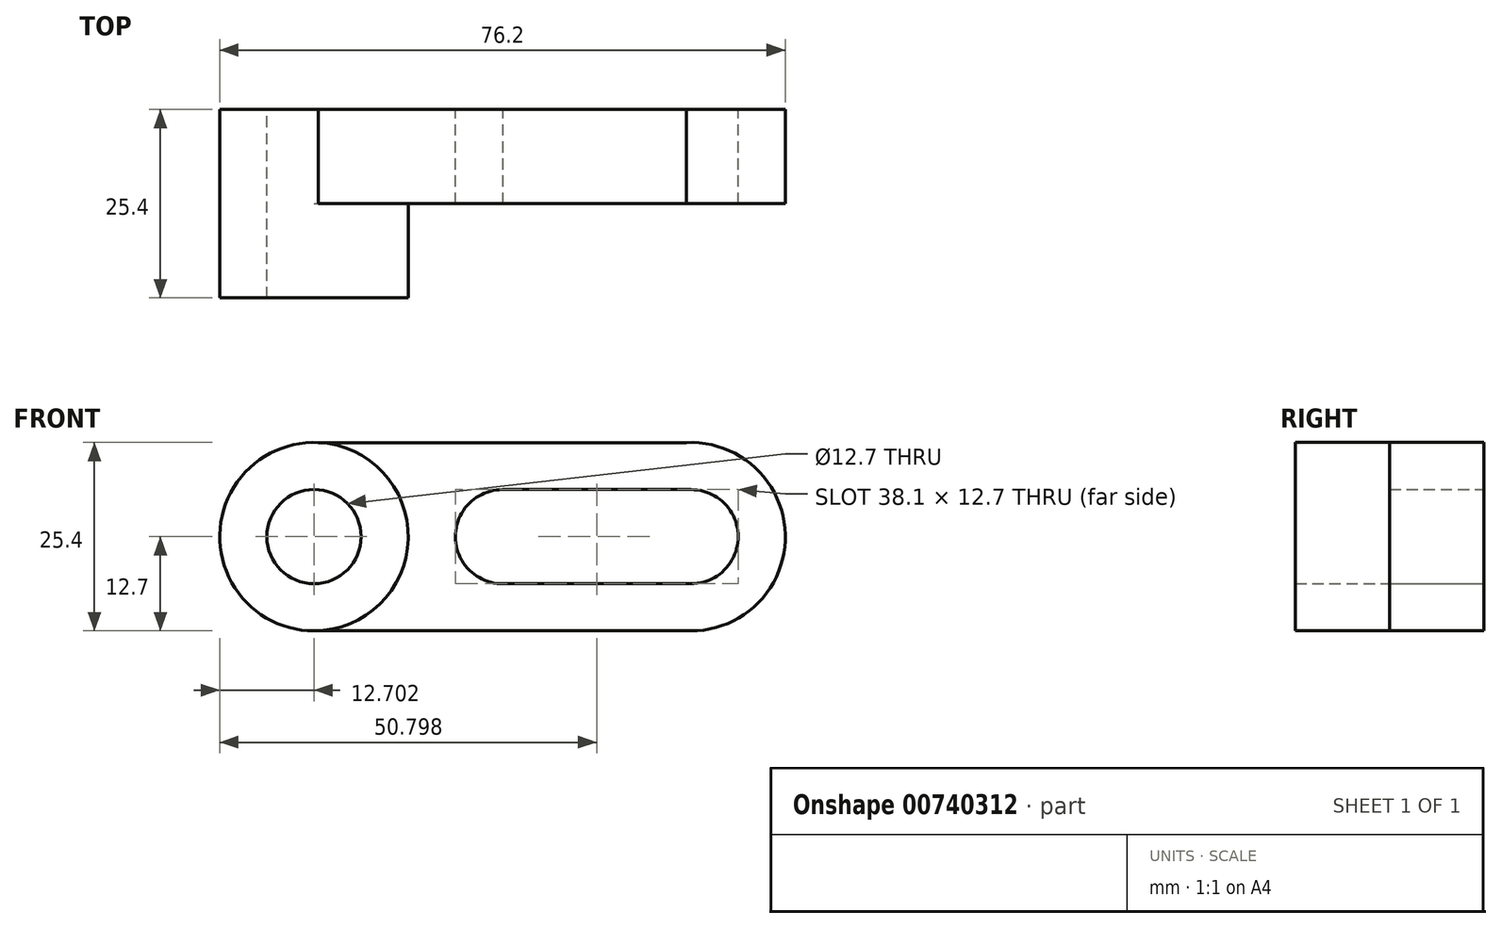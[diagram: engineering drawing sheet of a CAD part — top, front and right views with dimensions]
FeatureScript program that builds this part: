
annotation { "Feature Type Name" : "Feature", "Feature Type Description" : "" }
export const myFeature = defineFeature(function(context is Context, id is Id, definition is map)
    precondition{}
    {
        {
            var Q0;
            Q0=qCreatedBy(makeId("Front.planeOp"),FACE);
            var sketch = newSketch(context, id + "F0", { "sketchPlane" : qUnion([Q0])});
            skCircle(sketch, "E0", {"center": v(-18.11, 0) * mm, "radius": 12.7 * mm});
            skCircle(sketch, "E1", {"center": v(32.69, 0) * mm, "radius": 12.7 * mm});
            skLineSegment(sketch, "E2", {"start": v(-17.52, 12.69) * mm, "end": v(33.28, 12.69) * mm});
            skLineSegment(sketch, "E3", {"start": v(-18.11, -12.7) * mm, "end": v(32.69, -12.7) * mm});
            skSolve(sketch);
        }
        {
            var Q0;
            Q0 = qSketchRegion(id + "F0", true);
            extrude(context, id + "F1", {"entities" : qUnion([Q0]), "depth" : 12.7 * mm, "offsetDistance" : 25.4 * mm});
        }
        {
            var Q0;
            Q0=qCreatedBy(makeId("Front.planeOp"),FACE);
            var sketch = newSketch(context, id + "F2", { "sketchPlane" : qUnion([Q0])});
            skCircle(sketch, "E4", {"center": v(-18.1, 0) * mm, "radius": 12.7 * mm});
            skSolve(sketch);
        }
        {
            var Q0;
            Q0 = qSketchRegion(id + "F2", true);
            extrude(context, id + "F3", {"entities" : qUnion([Q0]), "operationType" : NewBodyOperationType.ADD, "depth" : 25.4 * mm, "offsetDistance" : 25.4 * mm});
        }
        {
            var Q0;
            Q0=qCreatedBy(makeId("Front.planeOp"),FACE);
            var sketch = newSketch(context, id + "F4", { "sketchPlane" : qUnion([Q0])});
            skCircle(sketch, "E5", {"center": v(-18.1, 0) * mm, "radius": 6.35 * mm});
            skSolve(sketch);
        }
        {
            var Q0;
            Q0 = qSketchRegion(id + "F4", true);
            extrude(context, id + "F5", {"entities" : qUnion([Q0]), "operationType" : NewBodyOperationType.REMOVE, "endBound" : BoundingType.THROUGH_ALL, "depth" : 25.4 * mm, "offsetDistance" : 25.4 * mm});
        }
        {
            var Q0;
            Q0=qCreatedBy(makeId("Front.planeOp"),FACE);
            var sketch = newSketch(context, id + "F6", { "sketchPlane" : qUnion([Q0])});
            skCircle(sketch, "E6", {"center": v(32.69, 0) * mm, "radius": 6.35 * mm});
            skCircle(sketch, "E7", {"center": v(7.29, 0) * mm, "radius": 6.35 * mm});
            skLineSegment(sketch, "E8", {"start": v(7.27, 6.35) * mm, "end": v(32.69, 6.35) * mm});
            skLineSegment(sketch, "E9", {"start": v(7.36, -6.35) * mm, "end": v(32.69, -6.35) * mm});
            skSolve(sketch);
        }
        {
            var Q0;
            Q0 = qSketchRegion(id + "F6", true);
            extrude(context, id + "F7", {"entities" : qUnion([Q0]), "operationType" : NewBodyOperationType.REMOVE, "endBound" : BoundingType.THROUGH_ALL, "depth" : 25.4 * mm, "offsetDistance" : 25.4 * mm});
        }
    });
